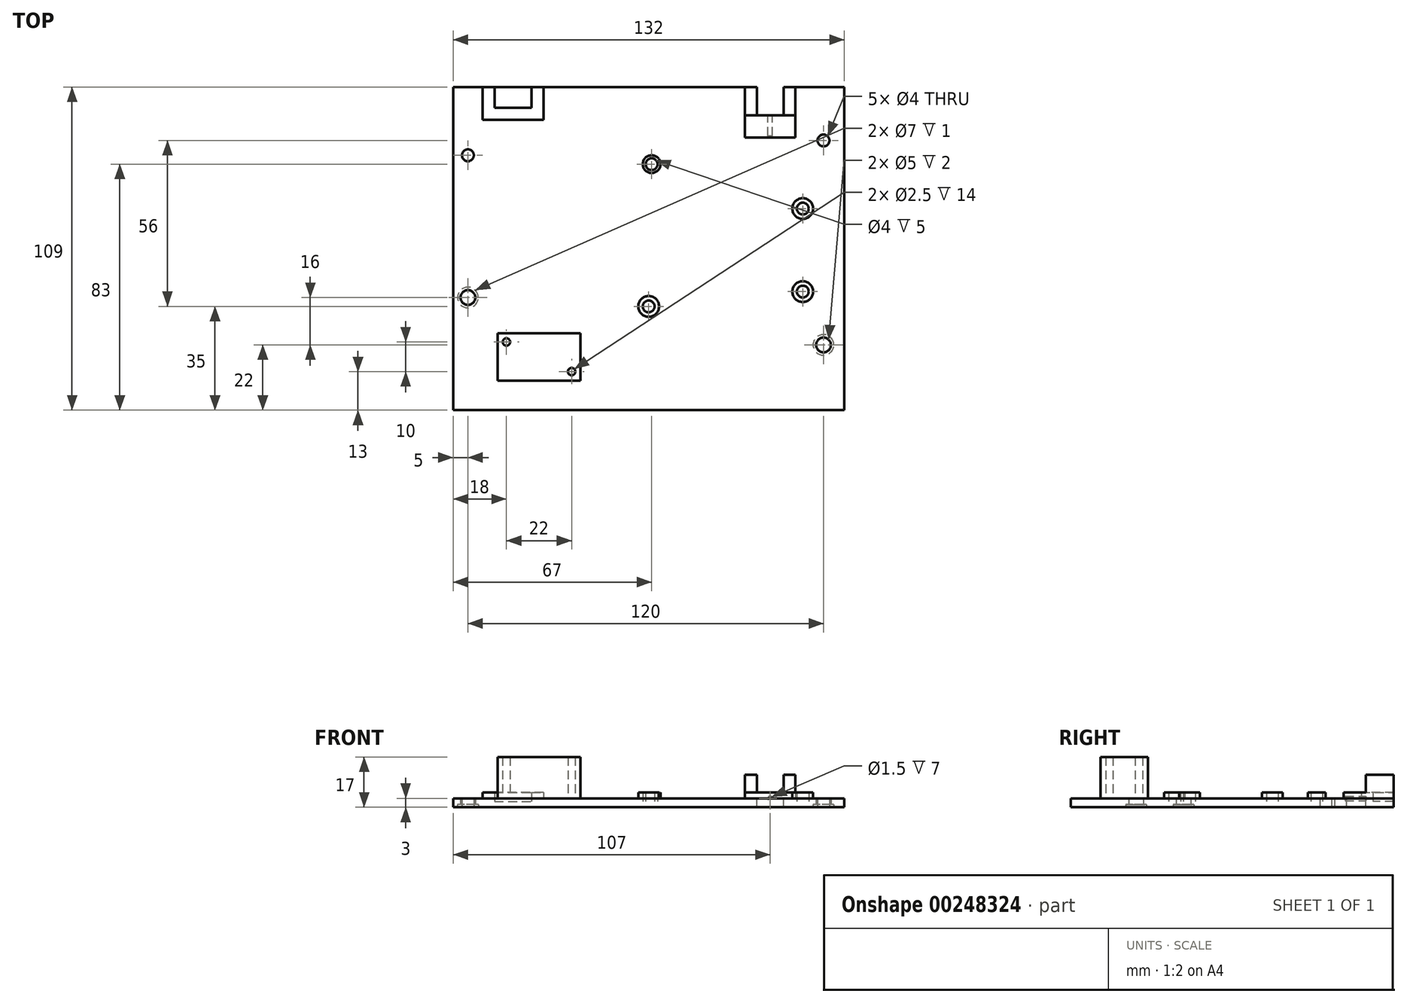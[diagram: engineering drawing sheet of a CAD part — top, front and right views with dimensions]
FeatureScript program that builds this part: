
annotation { "Feature Type Name" : "Feature", "Feature Type Description" : "" }
export const myFeature = defineFeature(function(context is Context, id is Id, definition is map)
    precondition{}
    {
        {
            var Q0;
            Q0=qCreatedBy(makeId("Top.planeOp"),FACE);
            var sketch = newSketch(context, id + "F0", { "sketchPlane" : qUnion([Q0])});
            skLineSegment(sketch, "E0.bottom", {"start": v(0, 0) * mm, "end": v(132, 0) * mm});
            skLineSegment(sketch, "E0.top", {"start": v(0, 109) * mm, "end": v(132, 109) * mm});
            skLineSegment(sketch, "E0.left", {"start": v(0, 0) * mm, "end": v(0, 109) * mm});
            skLineSegment(sketch, "E0.right", {"start": v(132, 0) * mm, "end": v(132, 109) * mm});
            skLineSegment(sketch, "E1", {"start": v(5, 109) * mm, "end": v(5, 0) * mm, "construction": true});
            skLineSegment(sketch, "E2", {"start": v(125, 109) * mm, "end": v(125, 60.2) * mm, "construction": true});
            skLineSegment(sketch, "E3", {"start": v(125, 0) * mm, "end": v(125, 33.82) * mm, "construction": true});
            skLineSegment(sketch, "E4", {"start": v(118, 81.57) * mm, "end": v(118, 11.83) * mm, "construction": true});
            skLineSegment(sketch, "E5", {"start": v(66, 40.1) * mm, "end": v(66, 3.03) * mm, "construction": true});
            skLineSegment(sketch, "E6", {"start": v(120.28, 91) * mm, "end": v(132, 91) * mm, "construction": true});
            skLineSegment(sketch, "E7", {"start": v(120.28, 22) * mm, "end": v(135.99, 22) * mm, "construction": true});
            skLineSegment(sketch, "E8", {"start": v(-4.13, 38) * mm, "end": v(16.6, 38) * mm, "construction": true});
            skLineSegment(sketch, "E9", {"start": v(-2.56, 86) * mm, "end": v(16.6, 86) * mm, "construction": true});
            skLineSegment(sketch, "E10", {"start": v(60.6, 83) * mm, "end": v(75.67, 83) * mm, "construction": true});
            skLineSegment(sketch, "E11", {"start": v(59.33, 35) * mm, "end": v(83.21, 35) * mm, "construction": true});
            skLineSegment(sketch, "E12", {"start": v(114.94, 68) * mm, "end": v(125, 68) * mm, "construction": true});
            skLineSegment(sketch, "E13", {"start": v(67, 94.77) * mm, "end": v(67, 67.75) * mm, "construction": true});
            skLineSegment(sketch, "E14", {"start": v(116.02, 40) * mm, "end": v(120.31, 40) * mm, "construction": true});
            skCircle(sketch, "E15", {"center": v(5, 86) * mm, "radius": 2 * mm});
            skCircle(sketch, "E16", {"center": v(5, 38) * mm, "radius": 3.5 * mm});
            skCircle(sketch, "E17", {"center": v(125, 91) * mm, "radius": 2 * mm});
            skCircle(sketch, "E18", {"center": v(125, 22) * mm, "radius": 3.5 * mm});
            skCircle(sketch, "E19", {"center": v(67, 83) * mm, "radius": 2 * mm});
            skCircle(sketch, "E20", {"center": v(66, 35) * mm, "radius": 2 * mm});
            skCircle(sketch, "E21", {"center": v(118, 40) * mm, "radius": 2 * mm});
            skCircle(sketch, "E22", {"center": v(118, 68) * mm, "radius": 2 * mm});
            skSolve(sketch);
        }
        {
            var Q0;
            Q0=makeQuery(id+"F0.imprint","IMPRINT",FACE,{"disambiguationData":[TD([[makeQuery(id+"F0.imprint","IMPRINT",EDGE,{"derivedFrom":sQuery(id+"F0.wireOp",EDGE,"E0.bottom")}),1.0]])]});
            extrude(context, id + "F1", {"entities" : qUnion([Q0]), "depth" : 1 * mm, "offsetDistance" : 25 * mm});
        }
        {
            var Q0;
            Q0=makeQuery(id+"F1.opExtrude","CAP_FACE",FACE,{"disambiguationData":[OSD([sQuery(id+"F0.wireOp",EDGE,"E0.bottom"),sQuery(id+"F0.wireOp",EDGE,"E0.top"),sQuery(id+"F0.wireOp",EDGE,"E0.left"),sQuery(id+"F0.wireOp",EDGE,"E0.right"),sQuery(id+"F0.wireOp",EDGE,"E15"),sQuery(id+"F0.wireOp",EDGE,"E16"),sQuery(id+"F0.wireOp",EDGE,"E17"),sQuery(id+"F0.wireOp",EDGE,"E18"),sQuery(id+"F0.wireOp",EDGE,"E19"),sQuery(id+"F0.wireOp",EDGE,"E20"),sQuery(id+"F0.wireOp",EDGE,"E21"),sQuery(id+"F0.wireOp",EDGE,"E22")])],"isStart":false});
            var sketch = newSketch(context, id + "F2", { "sketchPlane" : qUnion([Q0])});
            skLineSegment(sketch, "E23.0.0", {"start": v(132, 109) * mm, "end": v(0, 109) * mm});
            skLineSegment(sketch, "E23.0.1", {"start": v(0, 109) * mm, "end": v(0, 0) * mm});
            skLineSegment(sketch, "E23.0.2", {"start": v(0, 0) * mm, "end": v(132, 0) * mm});
            skLineSegment(sketch, "E23.0.3", {"start": v(132, 0) * mm, "end": v(132, 109) * mm});
            skLineSegment(sketch, "E24", {"start": v(120.43, 91) * mm, "end": v(130.8, 91) * mm, "construction": true});
            skLineSegment(sketch, "E25", {"start": v(125, 96.27) * mm, "end": v(125, 86.34) * mm, "construction": true});
            skLineSegment(sketch, "E26", {"start": v(125, 28.77) * mm, "end": v(125, 13.58) * mm, "construction": true});
            skLineSegment(sketch, "E27", {"start": v(120.4, 22) * mm, "end": v(131.51, 22) * mm, "construction": true});
            skCircle(sketch, "E28", {"center": v(125, 22) * mm, "radius": 2.5 * mm});
            skCircle(sketch, "E29", {"center": v(5, 38) * mm, "radius": 2.5 * mm});
            skSolve(sketch);
        }
        {
            var Q0;
            Q0=makeQuery(id+"F2.imprint","IMPRINT",FACE,{"disambiguationData":[TD([[makeQuery(id+"F2.imprint","IMPRINT",EDGE,{"derivedFrom":sQuery(id+"F2.wireOp",EDGE,"E28")}),-1.0]])]});
            var Q1;
            Q1=makeQuery(id+"F2.imprint","IMPRINT",FACE,{"disambiguationData":[TD([[makeQuery(id+"F2.imprint","IMPRINT",EDGE,{"derivedFrom":sQuery(id+"F2.wireOp",EDGE,"yfuNHKm1-oZ3f-3oQu-vYvV-wxrKH3D8ouKf")}),-1.0]])]});
            var Q2;
            Q2=makeQuery(id+"F2.imprint","IMPRINT",FACE,{"disambiguationData":[TD([[makeQuery(id+"F2.imprint","IMPRINT",EDGE,{"derivedFrom":sQuery(id+"F2.wireOp",EDGE,"E23.0.0")}),-1.0]])]});
            var Q3;
            Q3=makeQuery(id+"F2.imprint","IMPRINT",FACE,{"disambiguationData":[TD([[makeQuery(id+"F2.imprint","IMPRINT",EDGE,{"derivedFrom":sQuery(id+"F2.wireOp",EDGE,"E29")}),-1.0]])]});
            extrude(context, id + "F3", {"entities" : qUnion([Q0, Q1, Q2, Q3]), "operationType" : NewBodyOperationType.ADD, "depth" : 1 * mm, "offsetDistance" : 25 * mm});
        }
        {
            var Q0;
            Q0=makeQuery(id+"F3.opExtrude","CAP_FACE",FACE,{"disambiguationData":[OSD([sQuery(id+"F0.wireOp",EDGE,"E15"),sQuery(id+"F0.wireOp",EDGE,"E16"),sQuery(id+"F0.wireOp",EDGE,"E19"),sQuery(id+"F0.wireOp",EDGE,"E20"),sQuery(id+"F0.wireOp",EDGE,"E21"),sQuery(id+"F0.wireOp",EDGE,"E22"),sQuery(id+"F2.wireOp",EDGE,"E23.0.0"),sQuery(id+"F2.wireOp",EDGE,"E23.0.1"),sQuery(id+"F2.wireOp",EDGE,"E23.0.2"),sQuery(id+"F2.wireOp",EDGE,"E23.0.3"),sQuery(id+"F2.wireOp",EDGE,"yfuNHKm1-oZ3f-3oQu-vYvV-wxrKH3D8ouKf"),sQuery(id+"F2.wireOp",EDGE,"E28")])],"isStart":false});
            var sketch = newSketch(context, id + "F4", { "sketchPlane" : qUnion([Q0])});
            skLineSegment(sketch, "E30", {"start": v(14, 109) * mm, "end": v(14, 102) * mm});
            skLineSegment(sketch, "E31", {"start": v(14, 102) * mm, "end": v(26.5, 102) * mm});
            skLineSegment(sketch, "E32", {"start": v(26.5, 102) * mm, "end": v(26.5, 109) * mm});
            skSolve(sketch);
        }
        {
            var Q0;
            {var subQ1=sQuery(id+"F4.wireOp",EDGE,"E30");Q0=makeQuery(id+"F4.imprint","IMPRINT",FACE,{"disambiguationData":[TD([[makeQuery(id+"F4.imprint","IMPRINT",EDGE,{"derivedFrom":subQ1}),-1.0]])]});}
            var Q1;
            Q1 = qSketchRegion(id + "F6", true);
            extrude(context, id + "F5", {"entities" : qUnion([Q0, Q1]), "operationType" : NewBodyOperationType.ADD, "depth" : 1 * mm, "offsetDistance" : 25 * mm});
        }
        {
            var Q0;
            Q0=makeQuery(id+"F5.opExtrude","CAP_FACE",FACE,{"disambiguationData":[OSD([sQuery(id+"F0.wireOp",EDGE,"E15"),sQuery(id+"F0.wireOp",EDGE,"E16"),sQuery(id+"F0.wireOp",EDGE,"E19"),sQuery(id+"F0.wireOp",EDGE,"E20"),sQuery(id+"F0.wireOp",EDGE,"E21"),sQuery(id+"F0.wireOp",EDGE,"E22"),sQuery(id+"F2.wireOp",EDGE,"E23.0.0"),sQuery(id+"F2.wireOp",EDGE,"E23.0.1"),sQuery(id+"F2.wireOp",EDGE,"E23.0.2"),sQuery(id+"F2.wireOp",EDGE,"E23.0.3"),sQuery(id+"F2.wireOp",EDGE,"yfuNHKm1-oZ3f-3oQu-vYvV-wxrKH3D8ouKf"),sQuery(id+"F2.wireOp",EDGE,"E28"),sQuery(id+"F4.wireOp",EDGE,"E30"),sQuery(id+"F4.wireOp",EDGE,"E31"),sQuery(id+"F4.wireOp",EDGE,"E32")])],"isStart":false});
            var sketch = newSketch(context, id + "F6", { "sketchPlane" : qUnion([Q0])});
            skLineSegment(sketch, "E33", {"start": v(111.5, 109) * mm, "end": v(111.5, 99.5) * mm});
            skLineSegment(sketch, "E34", {"start": v(111.5, 99.5) * mm, "end": v(102.5, 99.5) * mm});
            skLineSegment(sketch, "E35", {"start": v(102.5, 99.5) * mm, "end": v(102.5, 109) * mm});
            skSolve(sketch);
        }
        {
            var Q0;
            {var subQ0=sQuery(id+"F6.wireOp",EDGE,"E33");Q0=makeQuery(id+"F6.imprint","IMPRINT",FACE,{"disambiguationData":[TD([[makeQuery(id+"F6.imprint","IMPRINT",EDGE,{"derivedFrom":subQ0}),-1.0]])]});}
            extrude(context, id + "F7", {"entities" : qUnion([Q0]), "operationType" : NewBodyOperationType.REMOVE, "oppositeDirection" : true, "depth" : 3 * mm, "offsetDistance" : 25 * mm});
        }
        {
            var Q0;
            Q0=makeQuery(id+"F5.opExtrude","CAP_FACE",FACE,{"disambiguationData":[OSD([sQuery(id+"F0.wireOp",EDGE,"E15"),sQuery(id+"F0.wireOp",EDGE,"E16"),sQuery(id+"F0.wireOp",EDGE,"E19"),sQuery(id+"F0.wireOp",EDGE,"E20"),sQuery(id+"F0.wireOp",EDGE,"E21"),sQuery(id+"F0.wireOp",EDGE,"E22"),sQuery(id+"F2.wireOp",EDGE,"E23.0.0"),sQuery(id+"F2.wireOp",EDGE,"E23.0.1"),sQuery(id+"F2.wireOp",EDGE,"E23.0.2"),sQuery(id+"F2.wireOp",EDGE,"E23.0.3"),sQuery(id+"F2.wireOp",EDGE,"yfuNHKm1-oZ3f-3oQu-vYvV-wxrKH3D8ouKf"),sQuery(id+"F2.wireOp",EDGE,"E28"),sQuery(id+"F4.wireOp",EDGE,"E30"),sQuery(id+"F4.wireOp",EDGE,"E31"),sQuery(id+"F4.wireOp",EDGE,"E32")])],"isStart":false});
            var sketch = newSketch(context, id + "F8", { "sketchPlane" : qUnion([Q0])});
            skLineSegment(sketch, "E36", {"start": v(14, 109) * mm, "end": v(14, 102) * mm});
            skLineSegment(sketch, "E37", {"start": v(14, 102) * mm, "end": v(26.5, 102) * mm});
            skLineSegment(sketch, "E38", {"start": v(26.5, 102) * mm, "end": v(26.5, 109) * mm});
            skLineSegment(sketch, "E39", {"start": v(26.5, 109) * mm, "end": v(30.5, 109) * mm});
            skLineSegment(sketch, "E40", {"start": v(30.5, 109) * mm, "end": v(30.5, 98) * mm});
            skLineSegment(sketch, "E41", {"start": v(30.5, 98) * mm, "end": v(10, 98) * mm});
            skLineSegment(sketch, "E42", {"start": v(10, 98) * mm, "end": v(10, 109) * mm});
            skLineSegment(sketch, "E43", {"start": v(102.5, 109) * mm, "end": v(102.5, 99.5) * mm});
            skLineSegment(sketch, "E44", {"start": v(102.5, 99.5) * mm, "end": v(111.5, 99.5) * mm});
            skLineSegment(sketch, "E45", {"start": v(111.5, 99.5) * mm, "end": v(111.5, 109) * mm});
            skLineSegment(sketch, "E46", {"start": v(111.5, 109) * mm, "end": v(115.5, 109) * mm});
            skLineSegment(sketch, "E47", {"start": v(115.5, 109) * mm, "end": v(115.5, 92) * mm});
            skLineSegment(sketch, "E48", {"start": v(115.5, 92) * mm, "end": v(98.5, 92) * mm});
            skLineSegment(sketch, "E49", {"start": v(98.5, 92) * mm, "end": v(98.5, 109) * mm});
            skCircle(sketch, "E50", {"center": v(67, 83) * mm, "radius": 3 * mm});
            skCircle(sketch, "E51", {"center": v(118, 68) * mm, "radius": 3.5 * mm});
            skCircle(sketch, "E52", {"center": v(118, 40) * mm, "radius": 3.5 * mm});
            skCircle(sketch, "E53", {"center": v(66, 35) * mm, "radius": 3.5 * mm});
            skLineSegment(sketch, "E54", {"start": v(132, 10) * mm, "end": v(0, 10) * mm});
            skLineSegment(sketch, "E55", {"start": v(15, 10) * mm, "end": v(15, 26) * mm});
            skLineSegment(sketch, "E56", {"start": v(15, 26) * mm, "end": v(43, 26) * mm});
            skLineSegment(sketch, "E57", {"start": v(43, 26) * mm, "end": v(43, 10) * mm});
            skLineSegment(sketch, "E58", {"start": v(13.97, 23) * mm, "end": v(20.38, 23) * mm, "construction": true});
            skLineSegment(sketch, "E59", {"start": v(18, 27.06) * mm, "end": v(18, 21.62) * mm, "construction": true});
            skLineSegment(sketch, "E60", {"start": v(44.5, 13) * mm, "end": v(38.14, 13) * mm, "construction": true});
            skLineSegment(sketch, "E61", {"start": v(40, 13.94) * mm, "end": v(40, 8.78) * mm, "construction": true});
            skCircle(sketch, "E62", {"center": v(18, 23) * mm, "radius": 1.25 * mm});
            skCircle(sketch, "E63", {"center": v(40, 13) * mm, "radius": 1.25 * mm});
            skSolve(sketch);
        }
        {
            var Q0;
            {var subQ0=sQuery(id+"F8.wireOp",EDGE,"E36");Q0=makeQuery(id+"F8.imprint","IMPRINT",FACE,{"disambiguationData":[TD([[makeQuery(id+"F8.imprint","IMPRINT",EDGE,{"derivedFrom":subQ0}),-1.0]])]});}
            var Q1;
            {var subQ0=sQuery(id+"F8.wireOp",EDGE,"E43");Q1=makeQuery(id+"F8.imprint","IMPRINT",FACE,{"disambiguationData":[TD([[makeQuery(id+"F8.imprint","IMPRINT",EDGE,{"derivedFrom":subQ0}),1.0]])]});}
            var Q2;
            Q2=makeQuery(id+"F8.imprint","IMPRINT",FACE,{"disambiguationData":[TD([[makeQuery(id+"F8.imprint","IMPRINT",EDGE,{"derivedFrom":sQuery(id+"F8.wireOp",EDGE,"E50")}),1.0]])]});
            var Q3;
            Q3=makeQuery(id+"F8.imprint","IMPRINT",FACE,{"disambiguationData":[TD([[makeQuery(id+"F8.imprint","IMPRINT",EDGE,{"derivedFrom":sQuery(id+"F8.wireOp",EDGE,"E53")}),1.0]])]});
            var Q4;
            Q4=makeQuery(id+"F8.imprint","IMPRINT",FACE,{"disambiguationData":[TD([[makeQuery(id+"F8.imprint","IMPRINT",EDGE,{"derivedFrom":sQuery(id+"F8.wireOp",EDGE,"E51")}),1.0]])]});
            var Q5;
            Q5=makeQuery(id+"F8.imprint","IMPRINT",FACE,{"disambiguationData":[TD([[makeQuery(id+"F8.imprint","IMPRINT",EDGE,{"derivedFrom":sQuery(id+"F8.wireOp",EDGE,"E52")}),1.0]])]});
            var Q6;
            {var subQ1=sQuery(id+"F8.wireOp",EDGE,"E55");Q6=makeQuery(id+"F8.imprint","IMPRINT",FACE,{"disambiguationData":[TD([[makeQuery(id+"F8.imprint","IMPRINT",EDGE,{"derivedFrom":subQ1}),-1.0]])]});}
            extrude(context, id + "F9", {"entities" : qUnion([Q0, Q1, Q2, Q3, Q4, Q5, Q6]), "operationType" : NewBodyOperationType.ADD, "depth" : 2 * mm, "offsetDistance" : 25 * mm});
        }
        {
            var Q0;
            Q0=makeQuery(id+"F9.opExtrude","CAP_FACE",FACE,{"disambiguationData":[OSD([sQuery(id+"F2.wireOp",EDGE,"E23.0.0"),sQuery(id+"F8.wireOp",EDGE,"E43"),sQuery(id+"F8.wireOp",EDGE,"E44"),sQuery(id+"F8.wireOp",EDGE,"E45"),sQuery(id+"F8.wireOp",EDGE,"E46"),sQuery(id+"F8.wireOp",EDGE,"E47"),sQuery(id+"F8.wireOp",EDGE,"E48"),sQuery(id+"F8.wireOp",EDGE,"E49")])],"isStart":false});
            var sketch = newSketch(context, id + "F10", { "sketchPlane" : qUnion([Q0])});
            skLineSegment(sketch, "E64", {"start": v(98.5, 109) * mm, "end": v(102.5, 109) * mm});
            skLineSegment(sketch, "E65", {"start": v(102.5, 109) * mm, "end": v(102.5, 99.5) * mm});
            skLineSegment(sketch, "E66", {"start": v(102.5, 99.5) * mm, "end": v(111.5, 99.5) * mm});
            skLineSegment(sketch, "E67", {"start": v(111.5, 99.5) * mm, "end": v(111.5, 109) * mm});
            skLineSegment(sketch, "E68", {"start": v(111.5, 109) * mm, "end": v(115.5, 109) * mm});
            skLineSegment(sketch, "E69", {"start": v(115.5, 109) * mm, "end": v(115.5, 99.5) * mm});
            skLineSegment(sketch, "E70", {"start": v(115.5, 99.5) * mm, "end": v(111.5, 99.5) * mm});
            skLineSegment(sketch, "E71", {"start": v(102.5, 99.5) * mm, "end": v(98.5, 99.5) * mm});
            skLineSegment(sketch, "E72", {"start": v(98.5, 99.5) * mm, "end": v(98.5, 109) * mm});
            skSolve(sketch);
        }
        {
            var Q0;
            Q0=makeQuery(id+"F10.imprint","IMPRINT",FACE,{"disambiguationData":[TD([[makeQuery(id+"F10.imprint","IMPRINT",EDGE,{"derivedFrom":sQuery(id+"F10.wireOp",EDGE,"E64")}),-1.0]])]});
            var Q1;
            Q1=makeQuery(id+"F10.imprint","IMPRINT",FACE,{"disambiguationData":[TD([[makeQuery(id+"F10.imprint","IMPRINT",EDGE,{"derivedFrom":sQuery(id+"F10.wireOp",EDGE,"E67")}),1.0]])]});
            var Q2;
            Q2=makeQuery(id+"F9.opExtrude","CAP_FACE",FACE,{"disambiguationData":[OSD([sQuery(id+"F8.wireOp",EDGE,"E54"),sQuery(id+"F8.wireOp",EDGE,"E55"),sQuery(id+"F8.wireOp",EDGE,"E56"),sQuery(id+"F8.wireOp",EDGE,"E57"),sQuery(id+"F8.wireOp",EDGE,"E62"),sQuery(id+"F8.wireOp",EDGE,"E63")])],"isStart":false});
            extrude(context, id + "F11", {"entities" : qUnion([Q0, Q1, Q2]), "operationType" : NewBodyOperationType.ADD, "depth" : 6 * mm, "offsetDistance" : 25 * mm});
        }
        {
            var Q0;
            Q0=makeQuery(id+"F9.boolean.opBoolean","MERGE",FACE,{"derivedFrom":[makeQuery(id+"F7.boolean.opBoolean","COPY",FACE,{"derivedFrom":makeQuery(id+"F7.opExtrude","SWEPT_FACE",FACE,{"disambiguationData":[OSD([sQuery(id+"F6.wireOp",EDGE,"E34")])]})}),makeQuery(id+"F9.opExtrude","SWEPT_FACE",FACE,{"disambiguationData":[OSD([sQuery(id+"F8.wireOp",EDGE,"E44")])]})]});
            var sketch = newSketch(context, id + "F12", { "sketchPlane" : qUnion([Q0])});
            skLineSegment(sketch, "E73", {"start": v(-111.5, 3) * mm, "end": v(-102.5, 3) * mm, "construction": true});
            skLineSegment(sketch, "E74", {"start": v(-107, 1.72) * mm, "end": v(-107, 5) * mm, "construction": true});
            skPoint(sketch, "E74.startSnap0", {"position": v(-107, 5) * mm});
            skCircle(sketch, "E75", {"center": v(-107, 3) * mm, "radius": 0.75 * mm});
            skSolve(sketch);
        }
        {
            var Q0;
            Q0 = qSketchRegion(id + "F12", true);
            extrude(context, id + "F13", {"entities" : qUnion([Q0]), "operationType" : NewBodyOperationType.REMOVE, "oppositeDirection" : true, "depth" : 7 * mm, "offsetDistance" : 25 * mm});
        }
        {
            var Q0;
            Q0=makeQuery(id+"F11.opExtrude","CAP_FACE",FACE,{"disambiguationData":[OSD([sQuery(id+"F8.wireOp",EDGE,"E54"),sQuery(id+"F8.wireOp",EDGE,"E55"),sQuery(id+"F8.wireOp",EDGE,"E56"),sQuery(id+"F8.wireOp",EDGE,"E57"),sQuery(id+"F8.wireOp",EDGE,"E62"),sQuery(id+"F8.wireOp",EDGE,"E63")])],"isStart":false});
            var sketch = newSketch(context, id + "F14", { "sketchPlane" : qUnion([Q0])});
            skSolve(sketch);
        }
        {
            var Q0;
            Q0=makeQuery(id+"F14.imprint","IMPRINT",FACE,{"disambiguationData":[TD([[makeQuery(id+"F14.imprint","IMPRINT",EDGE,{"derivedFrom":makeQuery(id+"F11.opExtrude","CAP_EDGE",EDGE,{"disambiguationData":[OSD([sQuery(id+"F8.wireOp",EDGE,"E54")])],"isStart":false})}),-1.0]])]});
            extrude(context, id + "F15", {"entities" : qUnion([Q0]), "operationType" : NewBodyOperationType.ADD, "depth" : 6 * mm, "offsetDistance" : 25 * mm});
        }
    });
